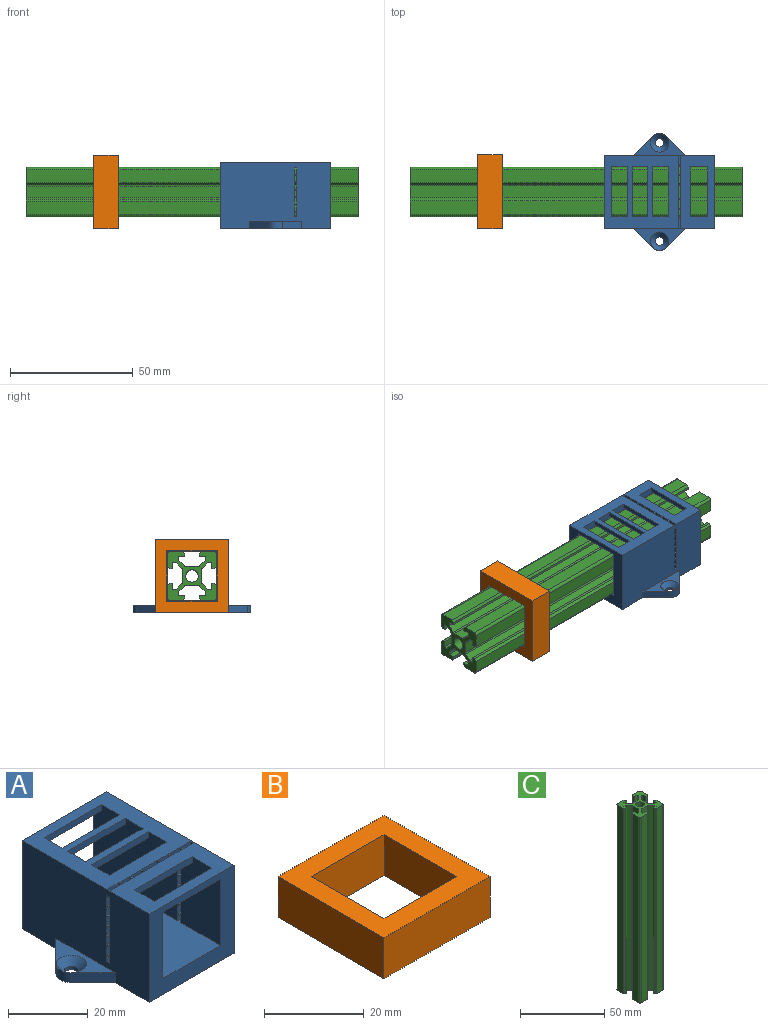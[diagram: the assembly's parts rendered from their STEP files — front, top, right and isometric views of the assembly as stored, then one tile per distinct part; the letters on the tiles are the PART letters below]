
ASSEMBLY  parts=3 mates=2
PART A: 118 faces, bbox 47.8x45x27 mm
  f0: plane 4.85x2.7mm, normal (0,-1,0), area 13.1mm2, adj f37,f59,f105,f116
  f1: plane 4.85x2.7mm, normal (0,1,0), area 13.1mm2, adj f37,f59,f105,f116
  f2: plane 8x1.93mm, normal (0,-1,0), area 14.1mm2, adj f37,f38,f39,f59,f96,f97,f98,f101
  f3: plane 8x1.93mm, normal (0,1,0), area 14.1mm2, adj f37,f38,f39,f59,f96,f97,f98,f101
  f4: plane 4.85x2.7mm, normal (0,-1,0), area 13.1mm2, adj f37,f59,f111,f112
  f5: plane 4.85x2.7mm, normal (0,1,0), area 13.1mm2, adj f37,f59,f111,f112
  f6: plane 4.85x2.7mm, normal (0,-1,0), area 13.1mm2, adj f37,f59,f110,f117
  f7: plane 4.85x2.7mm, normal (0,1,0), area 13.1mm2, adj f37,f59,f110,f117
  f8: plane 4.85x2.7mm, normal (0,-1,0), area 13.1mm2, adj f37,f59,f108,f113
  f9: plane 4.85x2.7mm, normal (0,1,0), area 13.1mm2, adj f37,f59,f108,f113
  f10: plane 3.7x1.85mm, normal (0,-1,0), area 6.8mm2, adj f38,f39,f107,f114
  f11: plane 3.7x1.85mm, normal (0,1,0), area 6.8mm2, adj f38,f39,f107,f114
  f12: plane 4.85x2.7mm, normal (0,-1,0), area 13.1mm2, adj f37,f59,f100,f104
  f13: plane 4.85x2.7mm, normal (0,1,0), area 13.1mm2, adj f37,f59,f100,f104
  f14: plane 5.4x1.85mm, normal (0,-1,0), area 10mm2, adj f38,f39,f94,f106
  f15: plane 4.85x1.93mm, normal (0,-1,0), area 9.3mm2, adj f37,f58,f59,f99
  f16: plane 4.85x1.93mm, normal (0,1,0), area 9.3mm2, adj f37,f58,f59,f99
  f17: plane 4.85x2.7mm, normal (0,-1,0), area 13.1mm2, adj f37,f59,f95,f109
  f18: plane 4.85x2.7mm, normal (0,1,0), area 13.1mm2, adj f37,f59,f95,f109
  f19: plane 5.4x1.85mm, normal (0,1,0), area 10mm2, adj f38,f39,f94,f106
  f20: plane 3.7x1.85mm, normal (0,-1,0), area 6.8mm2, adj f38,f39,f92,f93
  f21: plane 3.7x1.85mm, normal (0,1,0), area 6.8mm2, adj f38,f39,f92,f93
  f22: plane 8x1.93mm, normal (0,-1,0), area 14.1mm2, adj f36,f38,f39,f57,f85,f86,f87,f88
  f23: plane 8x1.93mm, normal (0,1,0), area 14.1mm2, adj f36,f38,f39,f57,f85,f86,f87,f88
  f24: plane 4.85x2.7mm, normal (0,-1,0), area 13.1mm2, adj f36,f57,f83,f84
  f25: plane 4.85x2.7mm, normal (0,1,0), area 13.1mm2, adj f36,f57,f83,f84
  f26: plane 4.85x2.7mm, normal (0,-1,0), area 13.1mm2, adj f36,f57,f81,f82
  f27: plane 4.85x2.7mm, normal (0,1,0), area 13.1mm2, adj f36,f57,f81,f82
  f28: plane 4.85x2.7mm, normal (0,-1,0), area 13.1mm2, adj f36,f57,f79,f80
  f29: plane 4.85x2.7mm, normal (0,1,0), area 13.1mm2, adj f36,f57,f79,f80
  f30: plane 4.85x2.7mm, normal (0,-1,0), area 13.1mm2, adj f36,f57,f77,f78
  f31: plane 4.85x2.7mm, normal (0,1,0), area 13.1mm2, adj f36,f57,f77,f78
  f32: plane 4.85x2.7mm, normal (0,-1,0), area 13.1mm2, adj f36,f57,f75,f76
  f33: plane 4.85x2.7mm, normal (0,1,0), area 13.1mm2, adj f36,f57,f75,f76
  f34: plane 4.85x2.7mm, normal (0,-1,0), area 13.1mm2, adj f36,f57,f73,f74
  f35: plane 4.85x2.7mm, normal (0,1,0), area 13.1mm2, adj f36,f57,f73,f74
  f36: plane 45x27mm, normal (-1,0,0), area 1133.8mm2, adj f22,f23,f24,f25,f26,f27,f28,f29
  f37: plane 45x27mm, normal (1,0,0), area 1133.8mm2, adj f0,f1,f2,f3,f4,f5,f6,f7
  f38: plane 45x30mm, normal (0,0,1), area 794.6mm2, adj f2,f3,f10,f11,f14,f19,f20,f21
  f39: plane 20.3x9mm, normal (0,0,-1), area 163.6mm2, adj f2,f3,f10,f11,f14,f19,f20,f21
  f40: plane 20.3x3mm, normal (0,0,-1), area 60.9mm2, adj f43,f57,f59,f66
  f41: plane 20.3x2mm, normal (0,0,-1), area 40.6mm2, adj f57,f59,f65,f67
  f42: plane 20.3x2mm, normal (0,0,-1), area 40.6mm2, adj f57,f59,f62,f64
  f43: plane 30x27mm, normal (0,1,0), area 397.9mm2, adj f36,f37,f38,f40,f45,f57,f58,f59
  f44: plane 30x27mm, normal (0,-1,0), area 397.9mm2, adj f36,f37,f38,f45,f56,f57,f58,f59
  f45: plane 47.77x45mm, normal (0,0,-1), area 1544.5mm2, adj f36,f37,f43,f44,f46,f47,f48,f49
  f46: plane 7.75x7.75mm, normal (-0.71,0.71,0), area 32.9mm2, adj f36,f45,f47,f50
  f47: cylinder r=3.88mm len=5.49mm, axis (0,0,-1), area 18.3mm2, adj f45,f46,f49,f50
  f48: cylinder r=1.75mm len=3.5mm, axis (0,0,-1), area 11mm2, adj f45,f70
  f49: plane 7.75x7.75mm, normal (-0.71,-0.71,0), area 32.9mm2, adj f36,f45,f47,f50
  f50: plane 20.98x8.88mm, normal (0,0,1), area 62.7mm2, adj f36,f46,f47,f49,f70
  f51: plane 7.75x7.75mm, normal (0.71,0.71,0), area 32.9mm2, adj f37,f45,f54,f55
  f52: plane 7.75x7.75mm, normal (0.71,-0.71,0), area 32.9mm2, adj f37,f45,f54,f55
  f53: cylinder r=1.75mm len=3.5mm, axis (0,0,-1), area 11mm2, adj f45,f71
  f54: cylinder r=3.88mm len=5.49mm, axis (0,0,-1), area 18.3mm2, adj f45,f51,f52,f55
  f55: plane 20.98x8.88mm, normal (0,0,1), area 62.7mm2, adj f37,f51,f52,f54,f71
  f56: plane 20.3x3mm, normal (0,0,-1), area 60.9mm2, adj f44,f57,f59,f69
  f57: plane 45x22.15mm, normal (1,0,0), area 943.4mm2, adj f22,f23,f24,f25,f26,f27,f28,f29
  f58: plane 45x30mm, normal (0,0,1), area 923.2mm2, adj f15,f16,f36,f37,f43,f44,f57,f59
  f59: plane 45x22.15mm, normal (-1,0,0), area 943.4mm2, adj f0,f1,f2,f3,f4,f5,f6,f7
  f60: plane 4.85x1.93mm, normal (0,-1,0), area 9.3mm2, adj f36,f57,f58,f72
  f61: plane 4.85x1.93mm, normal (0,1,0), area 9.3mm2, adj f36,f57,f58,f72
  f62: plane 20.3x1.85mm, normal (0,-1,0), area 37.6mm2, adj f38,f42,f57,f59
  f63: plane 20.3x1.85mm, normal (0,1,0), area 37.6mm2, adj f38,f39,f57,f59
  f64: plane 20.3x1.85mm, normal (0,1,0), area 37.6mm2, adj f38,f42,f57,f59
  f65: plane 20.3x1.85mm, normal (0,-1,0), area 37.6mm2, adj f38,f41,f57,f59
  f66: plane 20.3x1.85mm, normal (0,-1,0), area 37.6mm2, adj f38,f40,f57,f59
  f67: plane 20.3x1.85mm, normal (0,1,0), area 37.6mm2, adj f38,f41,f57,f59
  f68: plane 20.3x1.85mm, normal (0,-1,0), area 37.6mm2, adj f38,f39,f57,f59
  f69: plane 20.3x1.85mm, normal (0,1,0), area 37.6mm2, adj f38,f56,f57,f59
  f70: cone r=1.75mm half-angle=45deg, axis (0,0,1), area 48.9mm2, adj f48,f50
  f71: cone r=3.75mm half-angle=45deg, axis (0,0,1), area 48.9mm2, adj f53,f55
  f72: plane 4.85x1mm, normal (0,0,-1), area 4.9mm2, adj f36,f57,f60,f61
  f73: plane 4.85x1mm, normal (0,0,1), area 4.9mm2, adj f34,f35,f36,f57
  f74: plane 4.85x1mm, normal (0,0,-1), area 4.9mm2, adj f34,f35,f36,f57
  f75: plane 4.85x1mm, normal (0,0,1), area 4.9mm2, adj f32,f33,f36,f57
  f76: plane 4.85x1mm, normal (0,0,-1), area 4.9mm2, adj f32,f33,f36,f57
  f77: plane 4.85x1mm, normal (0,0,1), area 4.9mm2, adj f30,f31,f36,f57
  f78: plane 4.85x1mm, normal (0,0,-1), area 4.9mm2, adj f30,f31,f36,f57
  f79: plane 4.85x1mm, normal (0,0,1), area 4.9mm2, adj f28,f29,f36,f57
  f80: plane 4.85x1mm, normal (0,0,-1), area 4.9mm2, adj f28,f29,f36,f57
  f81: plane 4.85x1mm, normal (0,0,1), area 4.9mm2, adj f26,f27,f36,f57
  f82: plane 4.85x1mm, normal (0,0,-1), area 4.9mm2, adj f26,f27,f36,f57
  f83: plane 4.85x1mm, normal (0,0,1), area 4.9mm2, adj f24,f25,f36,f57
  f84: plane 4.85x1mm, normal (0,0,-1), area 4.9mm2, adj f24,f25,f36,f57
  f85: plane 4.85x1mm, normal (0,0,1), area 4.9mm2, adj f22,f23,f36,f57
  f86: plane 1.85x1mm, normal (1,0,0), area 1.9mm2, adj f22,f23,f38,f87
  f87: plane 1x0.3mm, normal (0,0,-1), area 0.3mm2, adj f22,f23,f36,f86
  f88: plane 1.85x1mm, normal (1,0,0), area 1.9mm2, adj f22,f23,f38,f90
  f89: plane 1.85x1mm, normal (-1,0,0), area 1.9mm2, adj f22,f23,f38,f90
  f90: plane 1x0.3mm, normal (0,0,-1), area 0.3mm2, adj f22,f23,f88,f89
  f91: plane 1.85x1mm, normal (-1,0,0), area 1.9mm2, adj f22,f23,f38,f39
  f92: plane 1.85x1mm, normal (1,0,0), area 1.9mm2, adj f20,f21,f38,f39
  f93: plane 1.85x1mm, normal (-1,0,0), area 1.9mm2, adj f20,f21,f38,f39
  f94: plane 1.85x1mm, normal (1,0,0), area 1.9mm2, adj f14,f19,f38,f39
  f95: plane 4.85x1mm, normal (0,0,-1), area 4.9mm2, adj f17,f18,f37,f59
  f96: plane 4.85x1mm, normal (0,0,1), area 4.9mm2, adj f2,f3,f37,f59
  f97: plane 1.85x1mm, normal (-1,0,0), area 1.9mm2, adj f2,f3,f38,f98
  f98: plane 1x0.3mm, normal (0,0,-1), area 0.3mm2, adj f2,f3,f37,f97
  f99: plane 4.85x1mm, normal (0,0,-1), area 4.9mm2, adj f15,f16,f37,f59
  f100: plane 4.85x1mm, normal (0,0,1), area 4.9mm2, adj f12,f13,f37,f59
  f101: plane 1.85x1mm, normal (-1,0,0), area 1.9mm2, adj f2,f3,f38,f103
  f102: plane 1.85x1mm, normal (1,0,0), area 1.9mm2, adj f2,f3,f38,f103
  f103: plane 1x0.3mm, normal (0,0,-1), area 0.3mm2, adj f2,f3,f101,f102
  f104: plane 4.85x1mm, normal (0,0,-1), area 4.9mm2, adj f12,f13,f37,f59
  f105: plane 4.85x1mm, normal (0,0,1), area 4.9mm2, adj f0,f1,f37,f59
  f106: plane 1.85x1mm, normal (-1,0,0), area 1.9mm2, adj f14,f19,f38,f39
  f107: plane 1.85x1mm, normal (1,0,0), area 1.9mm2, adj f10,f11,f38,f39
  f108: plane 4.85x1mm, normal (0,0,-1), area 4.9mm2, adj f8,f9,f37,f59
  f109: plane 4.85x1mm, normal (0,0,1), area 4.9mm2, adj f17,f18,f37,f59
  f110: plane 4.85x1mm, normal (0,0,-1), area 4.9mm2, adj f6,f7,f37,f59
  f111: plane 4.85x1mm, normal (0,0,1), area 4.9mm2, adj f4,f5,f37,f59
  f112: plane 4.85x1mm, normal (0,0,-1), area 4.9mm2, adj f4,f5,f37,f59
  f113: plane 4.85x1mm, normal (0,0,1), area 4.9mm2, adj f8,f9,f37,f59
  f114: plane 1.85x1mm, normal (-1,0,0), area 1.9mm2, adj f10,f11,f38,f39
  f115: plane 1.85x1mm, normal (1,0,0), area 1.9mm2, adj f2,f3,f38,f39
  f116: plane 4.85x1mm, normal (0,0,-1), area 4.9mm2, adj f0,f1,f37,f59
  f117: plane 4.85x1mm, normal (0,0,1), area 4.9mm2, adj f6,f7,f37,f59
PART B: 10 faces, bbox 30x30x10 mm
  f0: plane 30x10mm, normal (1,0,0), area 300mm2, adj f1,f7,f8,f9
  f1: plane 30x10mm, normal (0,1,0), area 300mm2, adj f0,f2,f8,f9
  f2: plane 30x10mm, normal (-1,0,0), area 300mm2, adj f1,f7,f8,f9
  f3: plane 20.5x10mm, normal (-1,0,0), area 205mm2, adj f4,f6,f8,f9
  f4: plane 20.5x10mm, normal (0,1,0), area 205mm2, adj f3,f5,f8,f9
  f5: plane 20.5x10mm, normal (1,0,0), area 205mm2, adj f4,f6,f8,f9
  f6: plane 20.5x10mm, normal (0,-1,0), area 205mm2, adj f3,f5,f8,f9
  f7: plane 30x10mm, normal (0,-1,0), area 300mm2, adj f0,f2,f8,f9
  f8: plane 30x30mm, normal (0,0,1), area 479.8mm2, adj f0,f1,f2,f3,f4,f5,f6,f7
  f9: plane 30x30mm, normal (0,0,-1), area 479.7mm2, adj f0,f1,f2,f3,f4,f5,f6,f7
PART C: 75 faces, bbox 20x20x135 mm
  f0: plane 135x1mm, normal (1,0,0), area 135mm2, adj f1,f71,f73,f74
  f1: plane 135x1mm, normal (0.82,0.57,0), area 164.8mm2, adj f0,f2,f73,f74
  f2: plane 135x5.3mm, normal (0,1,0), area 715.5mm2, adj f1,f3,f73,f74
  f3: cylinder r=1mm len=135mm, axis (0,0,-1), area 212.1mm2, adj f2,f4,f73,f74
  f4: plane 135x5.3mm, normal (-1,0,0), area 715.5mm2, adj f3,f5,f73,f74
  f5: plane 135x1mm, normal (-0.57,-0.82,0), area 164.8mm2, adj f4,f6,f73,f74
  f6: plane 135x1mm, normal (0,-1,0), area 135mm2, adj f5,f7,f73,f74
  f7: plane 135x2.5mm, normal (1,0,0), area 337.5mm2, adj f6,f8,f73,f74
  f8: plane 135x1.23mm, normal (0,-1,0), area 166.4mm2, adj f7,f9,f73,f74
  f9: cylinder r=0.5mm len=135mm, axis (0,0,-1), area 53mm2, adj f8,f10,f73,f74
  f10: plane 135x2.22mm, normal (-0.71,-0.71,0), area 424.1mm2, adj f9,f11,f73,f74
  f11: cylinder r=1mm len=135mm, axis (0,0,-1), area 106mm2, adj f10,f12,f73,f74
  f12: plane 135x4.85mm, normal (-1,0,0), area 654.8mm2, adj f11,f13,f73,f74
  f13: cylinder r=1mm len=135mm, axis (0,0,-1), area 106mm2, adj f12,f14,f73,f74
  f14: plane 135x2.22mm, normal (-0.71,0.71,0), area 424.1mm2, adj f13,f15,f73,f74
  f15: cylinder r=0.5mm len=135mm, axis (0,0,-1), area 53mm2, adj f14,f16,f73,f74
  f16: plane 135x1.23mm, normal (0,1,0), area 166.4mm2, adj f15,f17,f73,f74
  f17: plane 135x2.5mm, normal (1,0,0), area 337.5mm2, adj f16,f18,f73,f74
  f18: plane 135x1mm, normal (0,1,0), area 135mm2, adj f17,f19,f73,f74
  f19: plane 135x1mm, normal (-0.57,0.82,0), area 164.8mm2, adj f18,f20,f73,f74
  f20: plane 135x5.3mm, normal (-1,0,0), area 715.5mm2, adj f19,f21,f73,f74
  f21: cylinder r=1mm len=135mm, axis (0,0,-1), area 212.1mm2, adj f20,f22,f73,f74
  f22: plane 135x5.3mm, normal (0,-1,0), area 715.5mm2, adj f21,f23,f73,f74
  f23: plane 135x1mm, normal (0.82,-0.57,0), area 164.8mm2, adj f22,f24,f73,f74
  f24: plane 135x1mm, normal (1,0,0), area 135mm2, adj f23,f25,f73,f74
  f25: plane 135x2.5mm, normal (0,1,0), area 337.5mm2, adj f24,f26,f73,f74
  f26: plane 135x1.23mm, normal (1,0,0), area 166.4mm2, adj f25,f27,f73,f74
  f27: cylinder r=0.5mm len=135mm, axis (0,0,-1), area 53mm2, adj f26,f28,f73,f74
  f28: plane 135x2.22mm, normal (0.71,-0.71,0), area 424.1mm2, adj f27,f29,f73,f74
  f29: cylinder r=1mm len=135mm, axis (0,0,-1), area 106mm2, adj f28,f30,f73,f74
  f30: plane 135x4.85mm, normal (0,-1,0), area 654.8mm2, adj f29,f31,f73,f74
  f31: cylinder r=1mm len=135mm, axis (0,0,-1), area 106mm2, adj f30,f32,f73,f74
  f32: plane 135x2.22mm, normal (-0.71,-0.71,0), area 424.1mm2, adj f31,f33,f73,f74
  f33: cylinder r=0.5mm len=135mm, axis (0,0,-1), area 53mm2, adj f32,f34,f73,f74
  f34: plane 135x1.23mm, normal (-1,0,0), area 166.4mm2, adj f33,f35,f73,f74
  f35: plane 135x2.5mm, normal (0,1,0), area 337.5mm2, adj f34,f36,f73,f74
  f36: plane 135x1mm, normal (-1,0,0), area 135mm2, adj f35,f37,f73,f74
  f37: plane 135x1mm, normal (-0.82,-0.57,0), area 164.8mm2, adj f36,f38,f73,f74
  f38: plane 135x5.3mm, normal (0,-1,0), area 715.5mm2, adj f37,f39,f73,f74
  f39: cylinder r=1mm len=135mm, axis (0,0,-1), area 212.1mm2, adj f38,f40,f73,f74
  f40: plane 135x5.3mm, normal (1,0,0), area 715.5mm2, adj f39,f41,f73,f74
  f41: plane 135x1mm, normal (0.57,0.82,0), area 164.8mm2, adj f40,f42,f73,f74
  f42: plane 135x1mm, normal (0,1,0), area 135mm2, adj f41,f43,f73,f74
  f43: plane 135x2.5mm, normal (-1,0,0), area 337.5mm2, adj f42,f44,f73,f74
  f44: plane 135x1.23mm, normal (0,1,0), area 166.4mm2, adj f43,f45,f73,f74
  f45: cylinder r=0.5mm len=135mm, axis (0,0,-1), area 53mm2, adj f44,f46,f73,f74
  f46: plane 135x2.22mm, normal (0.71,0.71,0), area 424.1mm2, adj f45,f47,f73,f74
  f47: cylinder r=1mm len=135mm, axis (0,0,-1), area 106mm2, adj f46,f48,f73,f74
  f48: plane 135x4.85mm, normal (1,0,0), area 654.8mm2, adj f47,f49,f73,f74
  f49: cylinder r=1mm len=135mm, axis (0,0,-1), area 106mm2, adj f48,f50,f73,f74
  f50: plane 135x2.22mm, normal (0.71,-0.71,0), area 424.1mm2, adj f49,f51,f73,f74
  f51: cylinder r=0.5mm len=135mm, axis (0,0,-1), area 53mm2, adj f50,f52,f73,f74
  f52: plane 135x1.23mm, normal (0,-1,0), area 166.4mm2, adj f51,f53,f73,f74
  f53: plane 135x2.5mm, normal (-1,0,0), area 337.5mm2, adj f52,f54,f73,f74
  f54: plane 135x1mm, normal (0,-1,0), area 135mm2, adj f53,f55,f73,f74
  f55: plane 135x1mm, normal (0.57,-0.82,0), area 164.8mm2, adj f54,f56,f73,f74
  f56: plane 135x5.3mm, normal (1,0,0), area 715.5mm2, adj f55,f57,f73,f74
  f57: cylinder r=1mm len=135mm, axis (0,0,-1), area 212.1mm2, adj f56,f58,f73,f74
  f58: plane 135x5.3mm, normal (0,1,0), area 715.5mm2, adj f57,f59,f73,f74
  f59: plane 135x1mm, normal (-0.82,0.57,0), area 164.8mm2, adj f58,f60,f73,f74
  f60: plane 135x1mm, normal (-1,0,0), area 135mm2, adj f59,f61,f73,f74
  f61: plane 135x2.5mm, normal (0,-1,0), area 337.5mm2, adj f60,f62,f73,f74
  f62: plane 135x1.23mm, normal (-1,0,0), area 166.4mm2, adj f61,f63,f73,f74
  f63: cylinder r=0.5mm len=135mm, axis (0,0,-1), area 53mm2, adj f62,f64,f73,f74
  f64: plane 135x2.22mm, normal (-0.71,0.71,0), area 424.1mm2, adj f63,f65,f73,f74
  f65: cylinder r=1mm len=135mm, axis (0,0,-1), area 106mm2, adj f64,f66,f73,f74
  f66: plane 135x4.85mm, normal (0,1,0), area 654.8mm2, adj f65,f67,f73,f74
  f67: cylinder r=1mm len=135mm, axis (0,0,-1), area 106mm2, adj f66,f68,f73,f74
  f68: plane 135x2.22mm, normal (0.71,0.71,0), area 424.1mm2, adj f67,f69,f73,f74
  f69: cylinder r=0.5mm len=135mm, axis (0,0,-1), area 53mm2, adj f68,f70,f73,f74
  f70: plane 135x1.23mm, normal (1,0,0), area 166.4mm2, adj f69,f71,f73,f74
  f71: plane 135x2.5mm, normal (0,-1,0), area 337.5mm2, adj f0,f70,f73,f74
  f72: cylinder r=2.5mm len=135mm, axis (0,0,-1), area 2120.6mm2, adj f73,f74
  f73: plane 20x20mm, normal (0,0,1), area 176.8mm2, adj f0,f1,f2,f3,f4,f5,f6,f7
  f74: plane 20x20mm, normal (0,0,-1), area 176.8mm2, adj f0,f1,f2,f3,f4,f5,f6,f7
PLACE A rot(axis=(0,0,1),90deg) t=(-38.5,1.57,82.3)mm fixed
PLACE B rot(axis=(-0.58,-0.58,0.58),120deg) t=(-104.76,-52.91,97.3)mm
PLACE C rot(axis=(0,1,0),90deg) t=(-142.26,-52.91,122.3)mm
MATE slider C.f72 <-> A.f44  axis (1,0,0) through (-7.26,-52.91,97.3)mm
MATE fastened B.f8 <-> C.f72  axis (-1,0,0) through (-114.76,-52.91,97.3)mm
